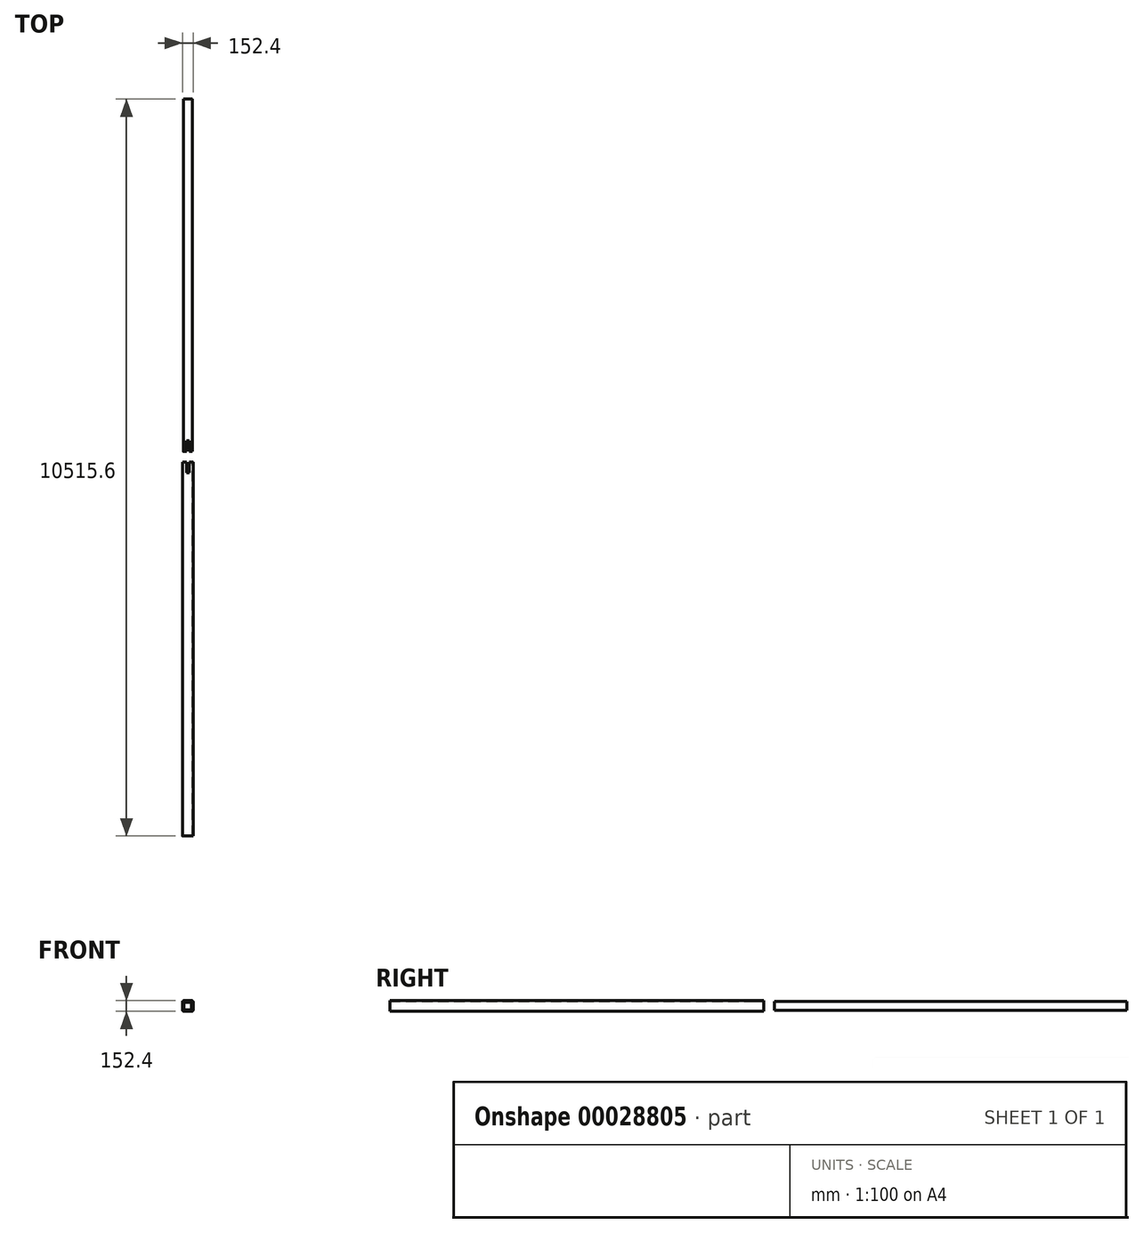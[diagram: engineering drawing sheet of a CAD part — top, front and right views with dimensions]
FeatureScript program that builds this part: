
annotation { "Feature Type Name" : "Feature", "Feature Type Description" : "" }
export const myFeature = defineFeature(function(context is Context, id is Id, definition is map)
    precondition{}
    {
        {
            var Q0;
            Q0=qCreatedBy(makeId("Front.planeOp"),FACE);
            var sketch = newSketch(context, id + "F0", { "sketchPlane" : qUnion([Q0])});
            skLineSegment(sketch, "E0.bottom", {"start": v(-57.15, 76.2) * mm, "end": v(57.15, 76.2) * mm});
            skLineSegment(sketch, "E0.top", {"start": v(-57.15, -76.2) * mm, "end": v(57.15, -76.2) * mm});
            skLineSegment(sketch, "E0.left", {"start": v(-76.2, 57.15) * mm, "end": v(-76.2, -57.15) * mm});
            skLineSegment(sketch, "E0.right", {"start": v(76.2, 57.15) * mm, "end": v(76.2, -57.15) * mm});
            skPoint(sketch, "E1.visualSharp", {"position": v(-76.2, 76.2) * mm});
            skArc(sketch, "E1.filletArc", {"start": v(-57.15, 76.2) * mm, "mid": v(-70.62, 70.62) * mm, "end": v(-76.2, 57.15) * mm});
            skPoint(sketch, "E2.visualSharp", {"position": v(76.2, 76.2) * mm});
            skArc(sketch, "E2.filletArc", {"start": v(76.2, 57.15) * mm, "mid": v(70.62, 70.62) * mm, "end": v(57.15, 76.2) * mm});
            skPoint(sketch, "E3.visualSharp", {"position": v(76.2, -76.2) * mm});
            skArc(sketch, "E3.filletArc", {"start": v(57.15, -76.2) * mm, "mid": v(70.62, -70.62) * mm, "end": v(76.2, -57.15) * mm});
            skPoint(sketch, "E4.visualSharp", {"position": v(-76.2, -76.2) * mm});
            skArc(sketch, "E4.filletArc", {"start": v(-76.2, -57.15) * mm, "mid": v(-70.62, -70.62) * mm, "end": v(-57.15, -76.2) * mm});
            skPoint(sketch, "E5.visualSharp", {"position": v(-70.04, -89.52) * mm});
            skPoint(sketch, "E6.visualSharp", {"position": v(-70.04, 53.33) * mm});
            skPoint(sketch, "E7.visualSharp", {"position": v(72.81, 53.33) * mm});
            skPoint(sketch, "E8.visualSharp", {"position": v(-66.67, 66.67) * mm});
            skPoint(sketch, "E9.visualSharp", {"position": v(66.67, 66.67) * mm});
            skPoint(sketch, "E10.visualSharp", {"position": v(-66.67, -66.67) * mm});
            skPoint(sketch, "E11.visualSharp", {"position": v(66.68, -66.67) * mm});
            skLineSegment(sketch, "E12.rect.bottom", {"start": v(-44.45, 63.5) * mm, "end": v(44.45, 63.5) * mm});
            skLineSegment(sketch, "E12.rect.top", {"start": v(-44.45, -63.5) * mm, "end": v(44.45, -63.5) * mm});
            skLineSegment(sketch, "E12.rect.left", {"start": v(-63.5, 44.45) * mm, "end": v(-63.5, -44.45) * mm});
            skLineSegment(sketch, "E12.rect.right", {"start": v(63.5, 44.45) * mm, "end": v(63.5, -44.45) * mm});
            skPoint(sketch, "E12.rect.middle", {"position": v(0, 0) * mm});
            skPoint(sketch, "E13.visualSharp", {"position": v(-63.5, 63.5) * mm});
            skArc(sketch, "E13.filletArc", {"start": v(-44.45, 63.5) * mm, "mid": v(-57.92, 57.92) * mm, "end": v(-63.5, 44.45) * mm});
            skPoint(sketch, "E14.visualSharp", {"position": v(-63.5, -63.5) * mm});
            skArc(sketch, "E14.filletArc", {"start": v(-63.5, -44.45) * mm, "mid": v(-57.92, -57.92) * mm, "end": v(-44.45, -63.5) * mm});
            skPoint(sketch, "E15.visualSharp", {"position": v(63.5, -63.5) * mm});
            skArc(sketch, "E15.filletArc", {"start": v(44.45, -63.5) * mm, "mid": v(57.92, -57.92) * mm, "end": v(63.5, -44.45) * mm});
            skPoint(sketch, "E16.visualSharp", {"position": v(63.5, 63.5) * mm});
            skArc(sketch, "E16.filletArc", {"start": v(63.5, 44.45) * mm, "mid": v(57.92, 57.92) * mm, "end": v(44.45, 63.5) * mm});
            skArc(sketch, "E17.0", {"start": v(-44.45, 53.98) * mm, "mid": v(-51.19, 51.19) * mm, "end": v(-53.98, 44.45) * mm});
            skLineSegment(sketch, "E17.1", {"start": v(-53.97, 44.45) * mm, "end": v(-53.97, -44.45) * mm});
            skLineSegment(sketch, "E17.2", {"start": v(-44.45, 53.98) * mm, "end": v(44.45, 53.98) * mm});
            skArc(sketch, "E17.3", {"start": v(-53.98, -44.45) * mm, "mid": v(-51.19, -51.19) * mm, "end": v(-44.45, -53.97) * mm});
            skArc(sketch, "E17.4", {"start": v(53.98, 44.45) * mm, "mid": v(51.19, 51.19) * mm, "end": v(44.45, 53.98) * mm});
            skLineSegment(sketch, "E17.5", {"start": v(53.98, 44.45) * mm, "end": v(53.98, -44.45) * mm});
            skArc(sketch, "E17.6", {"start": v(44.45, -53.97) * mm, "mid": v(51.19, -51.19) * mm, "end": v(53.98, -44.45) * mm});
            skLineSegment(sketch, "E17.7", {"start": v(-44.45, -53.98) * mm, "end": v(44.45, -53.98) * mm});
            skArc(sketch, "E18.0", {"start": v(-57.15, 66.67) * mm, "mid": v(-63.89, 63.89) * mm, "end": v(-66.68, 57.15) * mm});
            skLineSegment(sketch, "E18.1", {"start": v(-66.67, 57.15) * mm, "end": v(-66.67, -57.15) * mm});
            skLineSegment(sketch, "E18.2", {"start": v(-57.15, 66.67) * mm, "end": v(57.15, 66.67) * mm});
            skArc(sketch, "E18.3", {"start": v(-66.67, -57.15) * mm, "mid": v(-63.89, -63.89) * mm, "end": v(-57.15, -66.67) * mm});
            skArc(sketch, "E18.4", {"start": v(66.67, 57.15) * mm, "mid": v(63.89, 63.89) * mm, "end": v(57.15, 66.67) * mm});
            skLineSegment(sketch, "E18.5", {"start": v(66.67, 57.15) * mm, "end": v(66.67, -57.15) * mm});
            skArc(sketch, "E18.6", {"start": v(57.15, -66.67) * mm, "mid": v(63.89, -63.89) * mm, "end": v(66.68, -57.15) * mm});
            skLineSegment(sketch, "E18.7", {"start": v(-57.15, -66.67) * mm, "end": v(57.15, -66.67) * mm});
            skSolve(sketch);
        }
        {
            var Q0;
            Q0=makeQuery(id+"F0.imprint","IMPRINT",FACE,{"disambiguationData":[TD([[makeQuery(id+"F0.imprint","IMPRINT",EDGE,{"derivedFrom":sQuery(id+"F0.wireOp",EDGE,"E0.bottom")}),-1.0]])]});
            extrude(context, id + "F1", {"entities" : qUnion([Q0]), "depth" : 5334 * mm});
        }
        {
            var Q0;
            Q0=qCreatedBy(makeId("Front.planeOp"),FACE);
            cPlane(context, id + "F2", {"entities" : qUnion([Q0]), "cplaneType" : CPlaneType.OFFSET, "offset" : 152.4 * mm, "oppositeDirection" : true, "width" : 152.4 * mm, "height" : 152.4 * mm});
        }
        {
            var Q0;
            Q0=qCreatedBy(id+"F2.planeOp",FACE);
            var sketch = newSketch(context, id + "F3", { "sketchPlane" : qUnion([Q0])});
            skLineSegment(sketch, "E19.0", {"start": v(-44.45, 53.98) * mm, "end": v(44.45, 53.98) * mm});
            skLineSegment(sketch, "E20.0", {"start": v(-44.45, 63.5) * mm, "end": v(44.45, 63.5) * mm});
            skArc(sketch, "E21.0", {"start": v(63.5, 44.45) * mm, "mid": v(57.92, 57.92) * mm, "end": v(44.45, 63.5) * mm});
            skArc(sketch, "E22.0", {"start": v(53.98, 44.45) * mm, "mid": v(51.19, 51.19) * mm, "end": v(44.45, 53.98) * mm});
            skLineSegment(sketch, "E23.0", {"start": v(63.5, 44.45) * mm, "end": v(63.5, -44.45) * mm});
            skLineSegment(sketch, "E24.0", {"start": v(53.98, 44.45) * mm, "end": v(53.98, -44.45) * mm});
            skArc(sketch, "E25.0", {"start": v(44.45, -63.5) * mm, "mid": v(57.92, -57.92) * mm, "end": v(63.5, -44.45) * mm});
            skArc(sketch, "E26.0", {"start": v(44.45, -53.97) * mm, "mid": v(51.19, -51.19) * mm, "end": v(53.98, -44.45) * mm});
            skLineSegment(sketch, "E27.0", {"start": v(-44.45, -53.98) * mm, "end": v(44.45, -53.98) * mm});
            skLineSegment(sketch, "E28.0", {"start": v(-44.45, -63.5) * mm, "end": v(44.45, -63.5) * mm});
            skArc(sketch, "E29.0", {"start": v(-63.5, -44.45) * mm, "mid": v(-57.92, -57.92) * mm, "end": v(-44.45, -63.5) * mm});
            skArc(sketch, "E30.0", {"start": v(-53.98, -44.45) * mm, "mid": v(-51.19, -51.19) * mm, "end": v(-44.45, -53.97) * mm});
            skLineSegment(sketch, "E31.0", {"start": v(-53.97, 44.45) * mm, "end": v(-53.97, -44.45) * mm});
            skLineSegment(sketch, "E32.0", {"start": v(-63.5, 44.45) * mm, "end": v(-63.5, -44.45) * mm});
            skArc(sketch, "E33.0", {"start": v(-44.45, 53.98) * mm, "mid": v(-51.19, 51.19) * mm, "end": v(-53.98, 44.45) * mm});
            skArc(sketch, "E34.0", {"start": v(-44.45, 63.5) * mm, "mid": v(-57.92, 57.92) * mm, "end": v(-63.5, 44.45) * mm});
            skSolve(sketch);
        }
        {
            var Q0;
            Q0 = qSketchRegion(id + "F3", true);
            extrude(context, id + "F4", {"entities" : qUnion([Q0]), "oppositeDirection" : true, "depth" : 5029.2 * mm});
        }
        {
            var Q0;
            Q0=makeQuery(id+"F1.opExtrude","SWEPT_FACE",FACE,{"disambiguationData":[OSD([sQuery(id+"F0.wireOp",EDGE,"E0.bottom")])]});
            var sketch = newSketch(context, id + "F5", { "sketchPlane" : qUnion([Q0])});
            skLineSegment(sketch, "E35", {"start": v(-19.05, 0) * mm, "end": v(-19.05, -152.4) * mm});
            skLineSegment(sketch, "E36", {"start": v(-19.05, -152.4) * mm, "end": v(19.05, -152.4) * mm});
            skLineSegment(sketch, "E37", {"start": v(19.05, -152.4) * mm, "end": v(19.05, 0) * mm});
            skSolve(sketch);
        }
        {
            var Q0;
            {var subQ2=sQuery(id+"F5.wireOp",EDGE,"E35");Q0=makeQuery(id+"F5.imprint","IMPRINT",FACE,{"disambiguationData":[TD([[makeQuery(id+"F5.imprint","IMPRINT",EDGE,{"derivedFrom":subQ2}),1.0]])]});}
            extrude(context, id + "F6", {"entities" : qUnion([Q0]), "operationType" : NewBodyOperationType.REMOVE, "endBound" : BoundingType.THROUGH_ALL, "depth" : 25.4 * mm, "hasSecondDirection" : true, "secondDirectionBound" : SecondDirectionBoundingType.THROUGH_ALL, "secondDirectionOppositeDirection" : true, "secondDirectionDepth" : 25.4 * mm});
        }
        {
            var Q0;
            Q0=makeQuery(id+"F4.opExtrude","SWEPT_FACE",FACE,{"disambiguationData":[OSD([sQuery(id+"F3.wireOp",EDGE,"E20.0")])]});
            var sketch = newSketch(context, id + "F7", { "sketchPlane" : qUnion([Q0])});
            skLineSegment(sketch, "E38", {"start": v(-19.05, 152.4) * mm, "end": v(-19.05, 304.8) * mm});
            skLineSegment(sketch, "E39", {"start": v(-19.05, 304.8) * mm, "end": v(19.05, 304.8) * mm});
            skLineSegment(sketch, "E40", {"start": v(19.05, 304.8) * mm, "end": v(19.05, 152.4) * mm});
            skSolve(sketch);
        }
        {
            var Q0;
            {var subQ2=sQuery(id+"F7.wireOp",EDGE,"E38");Q0=makeQuery(id+"F7.imprint","IMPRINT",FACE,{"disambiguationData":[TD([[makeQuery(id+"F7.imprint","IMPRINT",EDGE,{"derivedFrom":subQ2}),-1.0]])]});}
            extrude(context, id + "F8", {"entities" : qUnion([Q0]), "operationType" : NewBodyOperationType.REMOVE, "endBound" : BoundingType.THROUGH_ALL, "oppositeDirection" : true, "depth" : 25.4 * mm, "hasSecondDirection" : true, "secondDirectionOppositeDirection" : false, "secondDirectionDepth" : 25.4 * mm});
        }
    });
